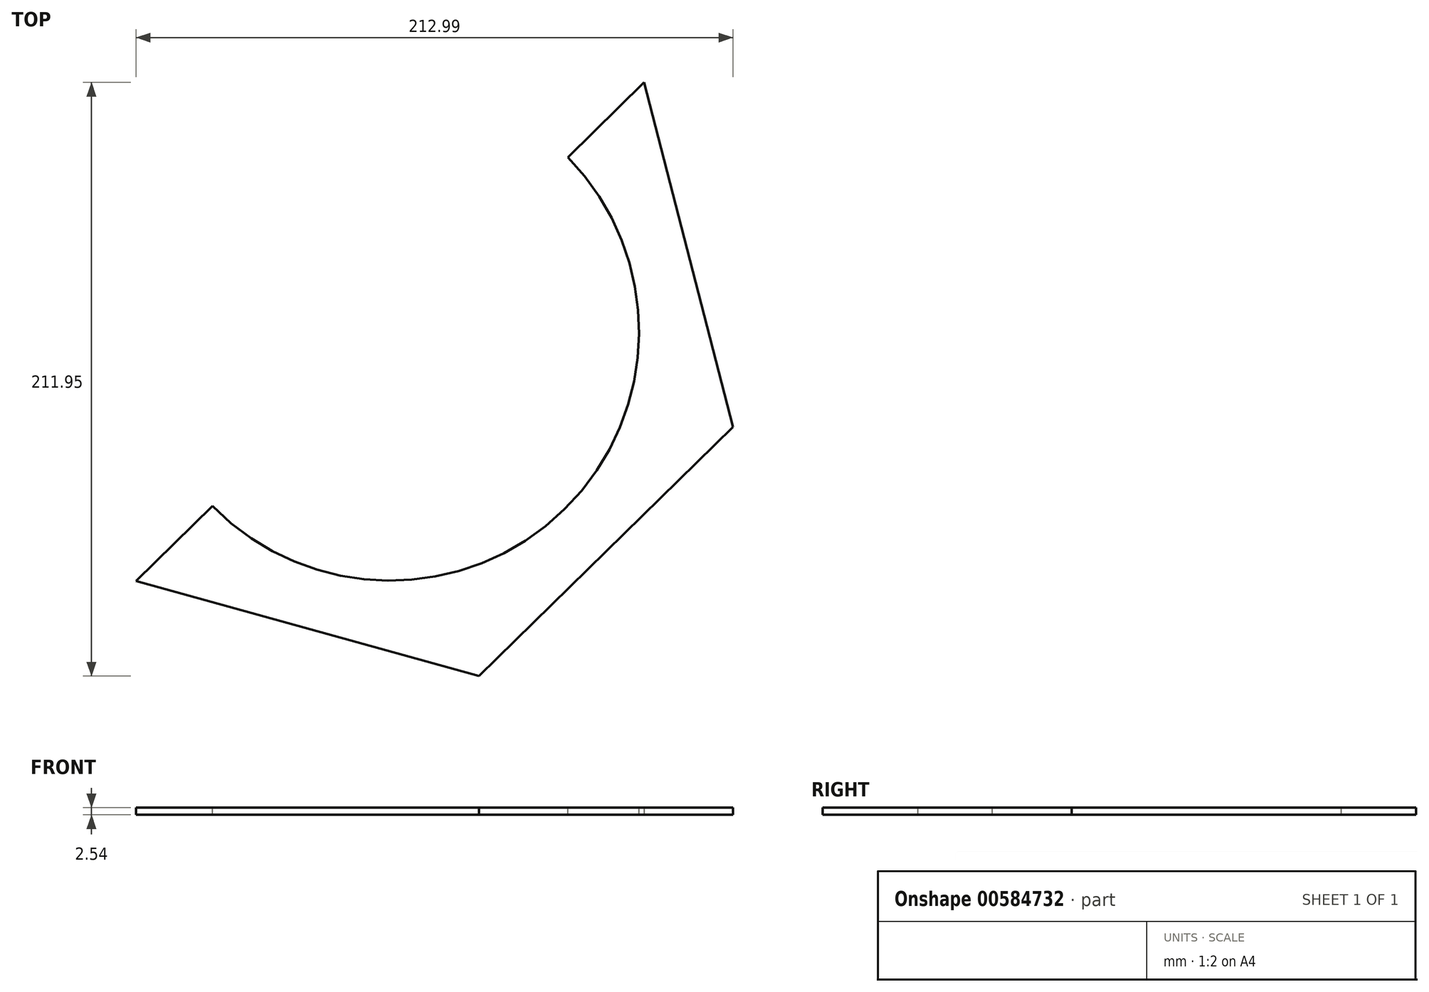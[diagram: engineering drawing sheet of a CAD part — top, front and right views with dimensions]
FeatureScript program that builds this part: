
annotation { "Feature Type Name" : "Feature", "Feature Type Description" : "" }
export const myFeature = defineFeature(function(context is Context, id is Id, definition is map)
    precondition{}
    {
        {
            var Q0;
            Q0=qCreatedBy(makeId("Top.planeOp"),FACE);
            var sketch = newSketch(context, id + "F0", { "sketchPlane" : qUnion([Q0])});
            skCircle(sketch, "E0.cCircle", {"center": v(0, 0) * mm, "radius": 109.99 * mm, "construction": true});
            skLineSegment(sketch, "E0.0", {"start": v(122.37, -33.99) * mm, "end": v(31.75, -122.97) * mm});
            skLineSegment(sketch, "E0.1", {"start": v(31.75, -122.97) * mm, "end": v(-90.62, -88.98) * mm});
            skLineSegment(sketch, "E0.2", {"start": v(-90.62, -88.98) * mm, "end": v(-122.37, 33.99) * mm});
            skLineSegment(sketch, "E0.3", {"start": v(-122.37, 33.99) * mm, "end": v(-31.75, 122.97) * mm});
            skLineSegment(sketch, "E0.4", {"start": v(-31.75, 122.97) * mm, "end": v(90.62, 88.98) * mm});
            skLineSegment(sketch, "E0.5", {"start": v(90.62, 88.98) * mm, "end": v(122.37, -33.99) * mm});
            skPoint(sketch, "E0.0.midPoint", {"position": v(77.06, -78.48) * mm});
            skSolve(sketch);
        }
        {
            var Q0;
            Q0 = qSketchRegion(id + "F0", true);
            extrude(context, id + "F1", {"entities" : qUnion([Q0]), "depth" : 2.54 * mm, "offsetDistance" : 25.4 * mm});
        }
        {
            var Q0;
            Q0=makeQuery(id+"F1.opExtrude","CAP_FACE",FACE,{"disambiguationData":[OSD([sQuery(id+"F0.wireOp",EDGE,"E0.0"),sQuery(id+"F0.wireOp",EDGE,"E0.1"),sQuery(id+"F0.wireOp",EDGE,"E0.2"),sQuery(id+"F0.wireOp",EDGE,"E0.3"),sQuery(id+"F0.wireOp",EDGE,"E0.4"),sQuery(id+"F0.wireOp",EDGE,"E0.5")])],"isStart":false});
            var sketch = newSketch(context, id + "F2", { "sketchPlane" : qUnion([Q0])});
            skLineSegment(sketch, "E1", {"start": v(90.62, 88.98) * mm, "end": v(-90.62, -88.98) * mm});
            skSolve(sketch);
        }
        {
            var Q0;
            {var subQ0=sQuery(id+"F2.wireOp",EDGE,"E1");Q0=makeQuery(id+"F2.imprint","IMPRINT",FACE,{"disambiguationData":[TD([[makeQuery(id+"F2.imprint","IMPRINT",EDGE,{"derivedFrom":subQ0}),-1.0]])]});}
            extrude(context, id + "F3", {"entities" : qUnion([Q0]), "operationType" : NewBodyOperationType.REMOVE, "oppositeDirection" : true, "depth" : 25.4 * mm, "offsetDistance" : 25.4 * mm});
        }
        {
            var Q0;
            Q0=makeQuery(id+"F1.opExtrude","CAP_FACE",FACE,{"disambiguationData":[OSD([sQuery(id+"F0.wireOp",EDGE,"E0.0"),sQuery(id+"F0.wireOp",EDGE,"E0.1"),sQuery(id+"F0.wireOp",EDGE,"E0.2"),sQuery(id+"F0.wireOp",EDGE,"E0.3"),sQuery(id+"F0.wireOp",EDGE,"E0.4"),sQuery(id+"F0.wireOp",EDGE,"E0.5")])],"isStart":false});
            var sketch = newSketch(context, id + "F4", { "sketchPlane" : qUnion([Q0])});
            skCircle(sketch, "E2", {"center": v(0, 0) * mm, "radius": 88.9 * mm});
            skSolve(sketch);
        }
        {
            var Q0;
            {var subQ0=sQuery(id+"F4.wireOp",EDGE,"E2");var subQ1=makeQuery(id+"F3.boolean.opBoolean","COPY",EDGE,{"derivedFrom":makeQuery(id+"F3.opExtrude","CAP_EDGE",EDGE,{"disambiguationData":[OSD([sQuery(id+"F2.wireOp",EDGE,"E1")])],"isStart":true})});var subQ2=makeQuery(id+"F4.imprint","INTERSECT",VERTEX,{"disambiguationData":[OD(0.0)],"derivedFrom":[subQ1,subQ0]});Q0=makeQuery(id+"F4.imprint","IMPRINT",FACE,{"disambiguationData":[TD([[makeQuery(id+"F4.imprint","IMPRINT",EDGE,{"disambiguationData":[TD([[subQ2,-1.0]])],"derivedFrom":subQ0}),1.0]])]});}
            extrude(context, id + "F5", {"entities" : qUnion([Q0]), "operationType" : NewBodyOperationType.REMOVE, "oppositeDirection" : true, "depth" : 25.4 * mm, "offsetDistance" : 25.4 * mm});
        }
    });
